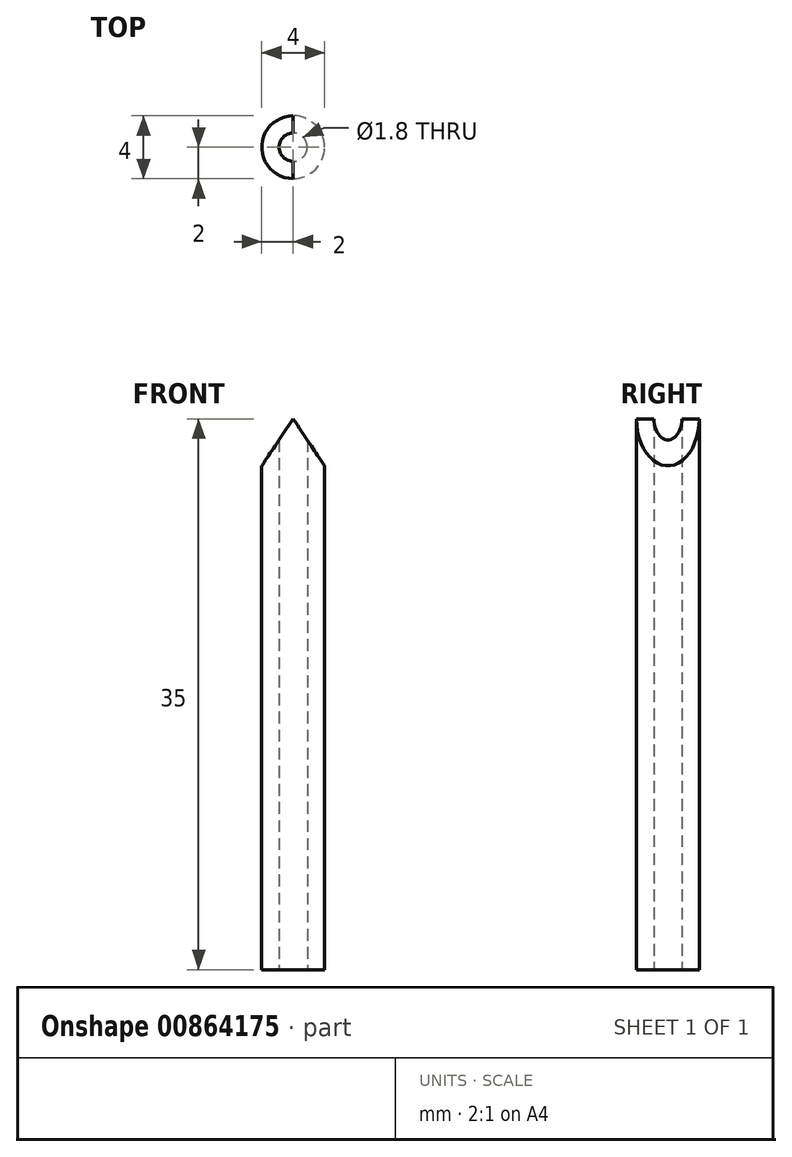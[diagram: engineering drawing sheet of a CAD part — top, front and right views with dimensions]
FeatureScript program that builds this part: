
annotation { "Feature Type Name" : "Feature", "Feature Type Description" : "" }
export const myFeature = defineFeature(function(context is Context, id is Id, definition is map)
    precondition{}
    {
        {
            var Q0;
            Q0=qCreatedBy(makeId("Top.planeOp"),FACE);
            var sketch = newSketch(context, id + "F0", { "sketchPlane" : qUnion([Q0])});
            skCircle(sketch, "E0", {"center": v(0, 0) * mm, "radius": 2 * mm});
            skCircle(sketch, "E1", {"center": v(0, 0) * mm, "radius": 0.9 * mm});
            skSolve(sketch);
        }
        {
            var Q0;
            Q0 = qSketchRegion(id + "F0", true);
            extrude(context, id + "F1", {"entities" : qUnion([Q0]), "depth" : 35 * mm, "offsetDistance" : 25 * mm});
        }
        {
            var Q0;
            Q0=qCreatedBy(makeId("Front.planeOp"),FACE);
            var sketch = newSketch(context, id + "F2", { "sketchPlane" : qUnion([Q0])});
            skLineSegment(sketch, "E2", {"start": v(0, 35) * mm, "end": v(2, 32) * mm});
            skLineSegment(sketch, "E3", {"start": v(2, 32) * mm, "end": v(2, 35) * mm});
            skLineSegment(sketch, "E4", {"start": v(2, 35) * mm, "end": v(0, 35) * mm});
            skLineSegment(sketch, "E5", {"start": v(0, 35) * mm, "end": v(0, 31.47) * mm, "construction": true});
            skLineSegment(sketch, "E6.MirrorCS", {"start": v(0, 35) * mm, "end": v(-2, 32) * mm});
            skLineSegment(sketch, "E7.MirrorCS", {"start": v(-2, 35) * mm, "end": v(0, 35) * mm});
            skLineSegment(sketch, "E8.MirrorCS", {"start": v(-2, 32) * mm, "end": v(-2, 35) * mm});
            skSolve(sketch);
        }
        {
            var Q0;
            Q0 = qSketchRegion(id + "F2", true);
            extrude(context, id + "F3", {"entities" : qUnion([Q0]), "operationType" : NewBodyOperationType.REMOVE, "endBound" : BoundingType.SYMMETRIC, "oppositeDirection" : true, "depth" : 25 * mm, "offsetDistance" : 25 * mm});
        }
    });
